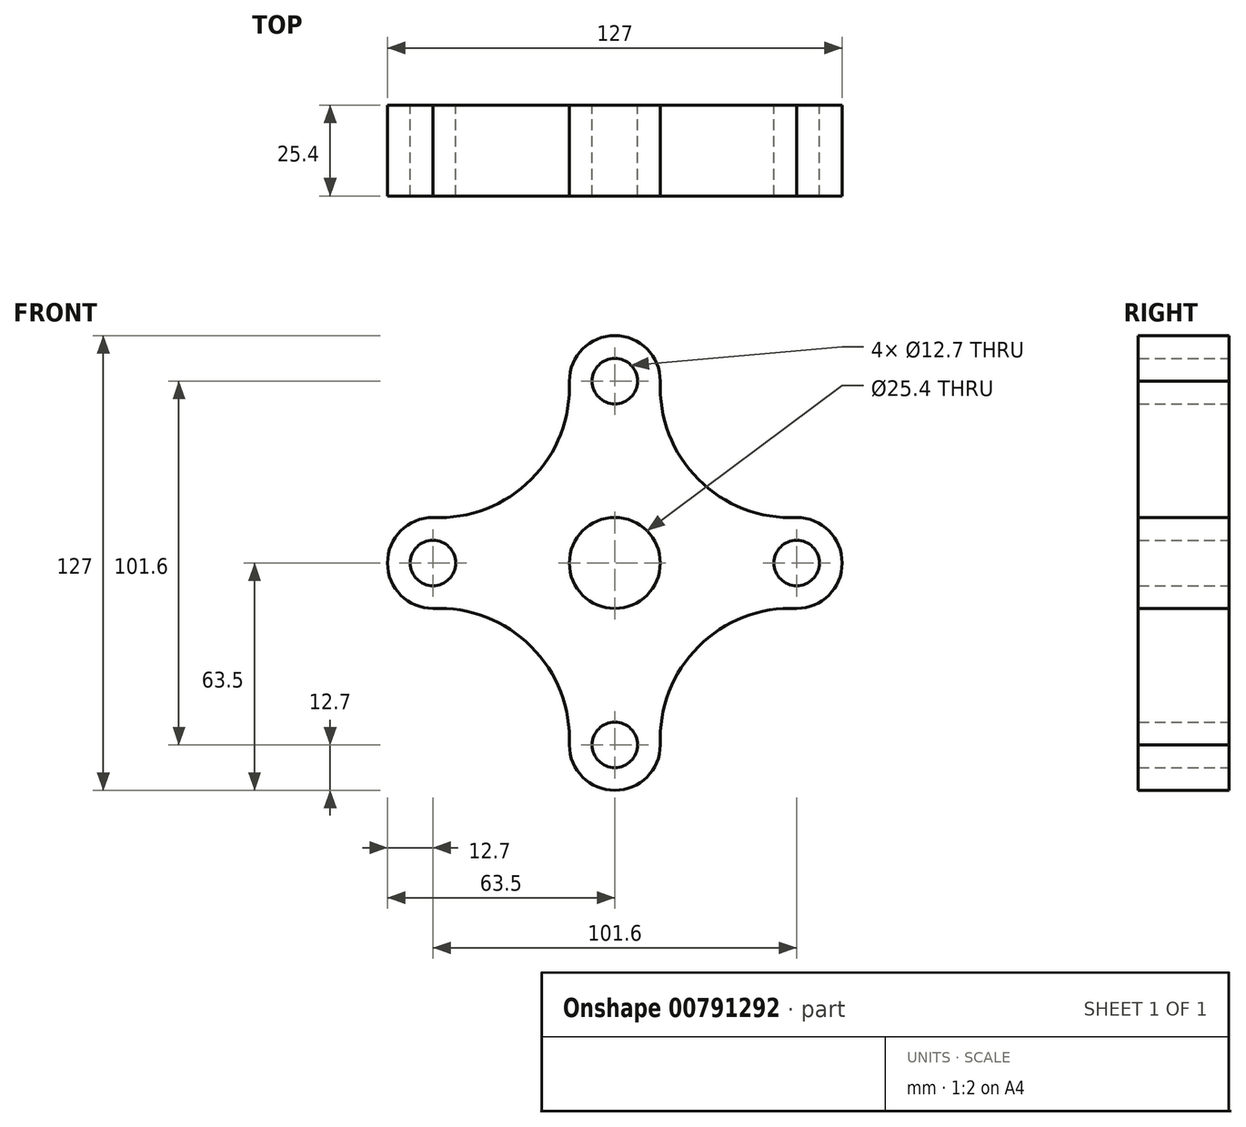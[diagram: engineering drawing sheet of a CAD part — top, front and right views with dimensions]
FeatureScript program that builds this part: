
annotation { "Feature Type Name" : "Feature", "Feature Type Description" : "" }
export const myFeature = defineFeature(function(context is Context, id is Id, definition is map)
    precondition{}
    {
        {
            var Q0;
            Q0=qCreatedBy(makeId("Front.planeOp"),FACE);
            var sketch = newSketch(context, id + "F0", { "sketchPlane" : qUnion([Q0])});
            skCircle(sketch, "E0", {"center": v(0, 0) * mm, "radius": 12.7 * mm});
            skLineSegment(sketch, "E1", {"start": v(0, 0) * mm, "end": v(0, 50.8) * mm});
            skCircle(sketch, "E2", {"center": v(0, 50.8) * mm, "radius": 6.35 * mm});
            skLineSegment(sketch, "E3", {"start": v(0, 0) * mm, "end": v(0, -50.8) * mm});
            skLineSegment(sketch, "E4", {"start": v(0, 0) * mm, "end": v(-50.8, 0) * mm});
            skLineSegment(sketch, "E5", {"start": v(0, 0) * mm, "end": v(50.8, 0) * mm});
            skCircle(sketch, "E6", {"center": v(-50.8, 0) * mm, "radius": 6.35 * mm});
            skCircle(sketch, "E7", {"center": v(0, -50.8) * mm, "radius": 6.35 * mm});
            skLineSegment(sketch, "E8", {"start": v(-50.8, 0) * mm, "end": v(-50.8, 12.7) * mm});
            skLineSegment(sketch, "E9", {"start": v(-50.8, 0) * mm, "end": v(-50.8, -12.7) * mm});
            skLineSegment(sketch, "E10", {"start": v(0, -50.8) * mm, "end": v(12.7, -50.8) * mm});
            skLineSegment(sketch, "E11", {"start": v(0, -50.8) * mm, "end": v(-12.7, -50.8) * mm});
            skLineSegment(sketch, "E12", {"start": v(0, 50.8) * mm, "end": v(12.7, 50.8) * mm});
            skLineSegment(sketch, "E13", {"start": v(0, 50.8) * mm, "end": v(-12.7, 50.8) * mm});
            skCircle(sketch, "E14", {"center": v(50.8, 0) * mm, "radius": 6.35 * mm});
            skLineSegment(sketch, "E15", {"start": v(50.8, 0) * mm, "end": v(50.8, 12.7) * mm});
            skLineSegment(sketch, "E16", {"start": v(50.8, 0) * mm, "end": v(50.8, -12.7) * mm});
            skArc(sketch, "E17", {"start": v(-50.8, 12.7) * mm, "mid": v(-63.5, 0) * mm, "end": v(-50.8, -12.7) * mm});
            skArc(sketch, "E18", {"start": v(12.7, 50.8) * mm, "mid": v(0, 63.5) * mm, "end": v(-12.7, 50.8) * mm});
            skArc(sketch, "E19", {"start": v(50.8, -12.7) * mm, "mid": v(63.5, 0) * mm, "end": v(50.8, 12.7) * mm});
            skArc(sketch, "E20", {"start": v(-12.7, -50.8) * mm, "mid": v(0, -63.5) * mm, "end": v(12.7, -50.8) * mm});
            skArc(sketch, "E21", {"start": v(-50.8, 12.7) * mm, "mid": v(-23.36, 23.36) * mm, "end": v(-12.7, 50.8) * mm});
            skArc(sketch, "E22", {"start": v(12.7, 50.8) * mm, "mid": v(23.36, 23.36) * mm, "end": v(50.8, 12.7) * mm});
            skArc(sketch, "E23", {"start": v(50.8, -12.7) * mm, "mid": v(23.36, -23.36) * mm, "end": v(12.7, -50.8) * mm});
            skArc(sketch, "E24", {"start": v(-12.7, -50.8) * mm, "mid": v(-23.36, -23.36) * mm, "end": v(-50.8, -12.7) * mm});
            skSolve(sketch);
        }
        {
            var Q0;
            Q0 = qSketchRegion(id + "F0", true);
            extrude(context, id + "F1", {"entities" : qUnion([Q0]), "depth" : 25.4 * mm, "offsetDistance" : 25.4 * mm});
        }
    });
